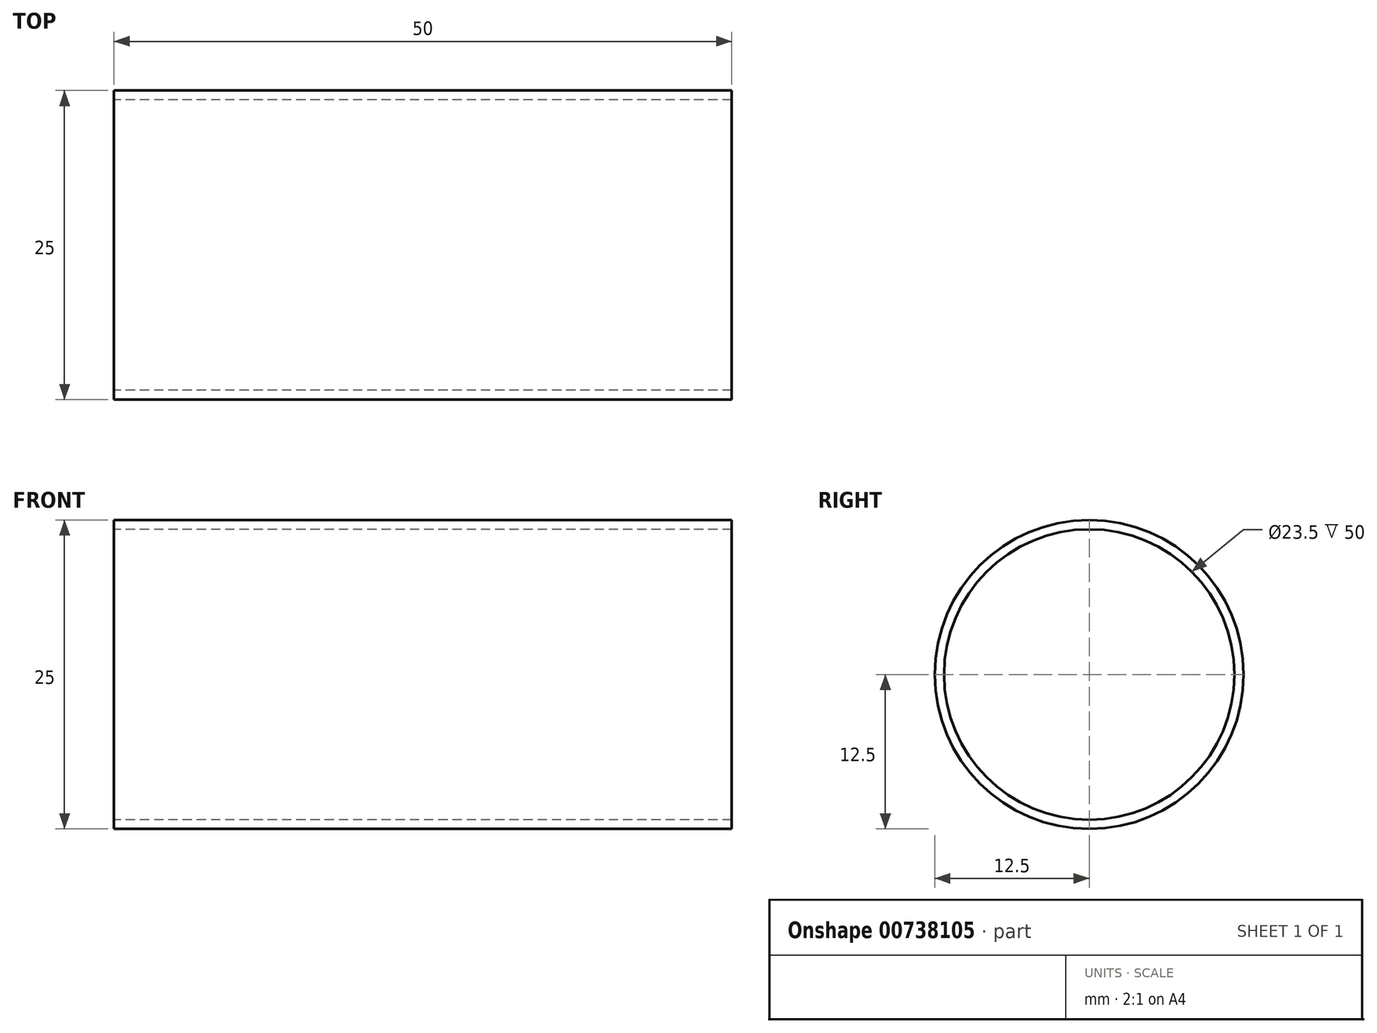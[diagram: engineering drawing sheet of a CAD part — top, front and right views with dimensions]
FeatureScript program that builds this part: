
annotation { "Feature Type Name" : "Feature", "Feature Type Description" : "" }
export const myFeature = defineFeature(function(context is Context, id is Id, definition is map)
    precondition{}
    {
        {
            var Q0;
            Q0=qCreatedBy(makeId("Right.planeOp"),FACE);
            var sketch = newSketch(context, id + "F0", { "sketchPlane" : qUnion([Q0])});
            skCircle(sketch, "E0", {"center": v(0, 0) * mm, "radius": 12.5 * mm});
            skCircle(sketch, "E1", {"center": v(0, 0) * mm, "radius": 11.75 * mm});
            skSolve(sketch);
        }
        {
            var Q0;
            Q0=makeQuery(id+"F0.imprint","IMPRINT",FACE,{"disambiguationData":[TD([[makeQuery(id+"F0.imprint","IMPRINT",EDGE,{"derivedFrom":sQuery(id+"F0.wireOp",EDGE,"E0")}),1.0]])]});
            extrude(context, id + "F1", {"entities" : qUnion([Q0]), "depth" : 50 * mm, "offsetDistance" : 25 * mm});
        }
    });
